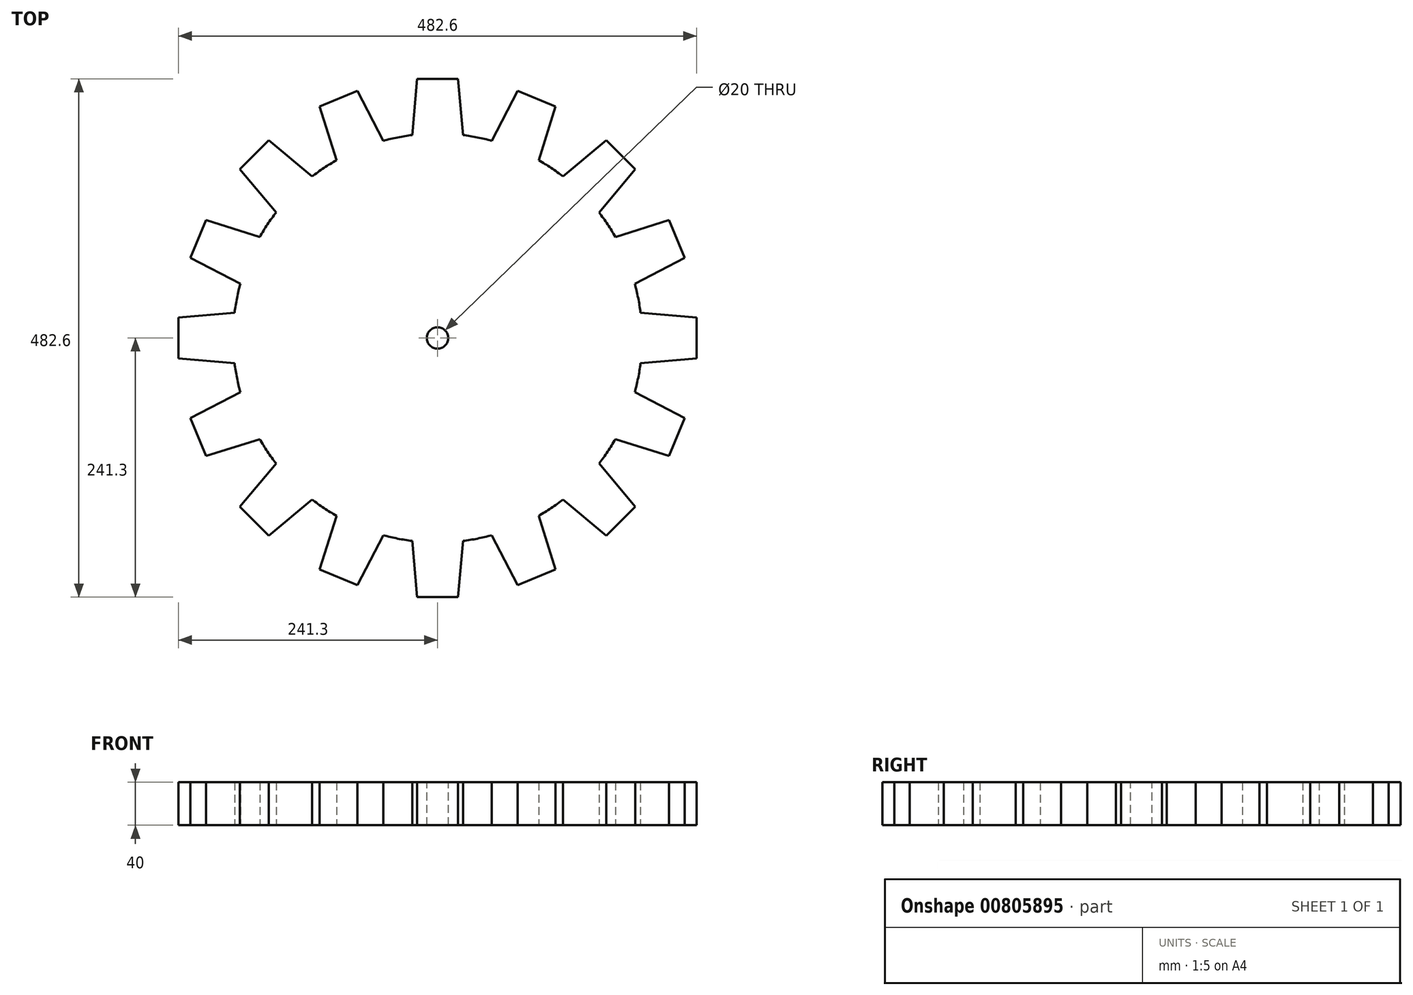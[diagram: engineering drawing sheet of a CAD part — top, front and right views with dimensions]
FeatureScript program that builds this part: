
annotation { "Feature Type Name" : "Feature", "Feature Type Description" : "" }
export const myFeature = defineFeature(function(context is Context, id is Id, definition is map)
    precondition{}
    {
        {
            var Q0;
            Q0=qCreatedBy(makeId("Top.planeOp"),FACE);
            var sketch = newSketch(context, id + "F0", { "sketchPlane" : qUnion([Q0])});
            skCircle(sketch, "E0", {"center": v(0, 0) * mm, "radius": 190.5 * mm});
            skLineSegment(sketch, "E1", {"start": v(0, 0) * mm, "end": v(0, 190.5) * mm, "construction": true});
            skLineSegment(sketch, "E2", {"start": v(-23.62, 189.03) * mm, "end": v(-19.05, 241.3) * mm});
            skLineSegment(sketch, "E3", {"start": v(-19.05, 241.3) * mm, "end": v(0, 241.3) * mm});
            skLineSegment(sketch, "E4.MirrorCS", {"start": v(23.62, 189.03) * mm, "end": v(19.05, 241.3) * mm});
            skLineSegment(sketch, "E5.MirrorCS", {"start": v(19.05, 241.3) * mm, "end": v(0, 241.3) * mm});
            skLineSegment(sketch, "E6.1.0", {"start": v(-94.16, 165.6) * mm, "end": v(-109.94, 215.64) * mm});
            skLineSegment(sketch, "E6.1.1", {"start": v(-109.94, 215.64) * mm, "end": v(-92.34, 222.93) * mm});
            skLineSegment(sketch, "E6.1.2", {"start": v(-74.74, 230.22) * mm, "end": v(-92.34, 222.93) * mm});
            skLineSegment(sketch, "E6.1.3", {"start": v(-50.51, 183.68) * mm, "end": v(-74.74, 230.22) * mm});
            skLineSegment(sketch, "E6.2.0", {"start": v(-150.37, 116.96) * mm, "end": v(-184.1, 157.15) * mm});
            skLineSegment(sketch, "E6.2.1", {"start": v(-184.1, 157.15) * mm, "end": v(-170.62, 170.62) * mm});
            skLineSegment(sketch, "E6.2.2", {"start": v(-157.15, 184.1) * mm, "end": v(-170.62, 170.62) * mm});
            skLineSegment(sketch, "E6.2.3", {"start": v(-116.96, 150.37) * mm, "end": v(-157.15, 184.1) * mm});
            skLineSegment(sketch, "E6.3.0", {"start": v(-183.68, 50.51) * mm, "end": v(-230.22, 74.74) * mm});
            skLineSegment(sketch, "E6.3.1", {"start": v(-230.22, 74.74) * mm, "end": v(-222.93, 92.34) * mm});
            skLineSegment(sketch, "E6.3.2", {"start": v(-215.64, 109.94) * mm, "end": v(-222.93, 92.34) * mm});
            skLineSegment(sketch, "E6.3.3", {"start": v(-165.6, 94.16) * mm, "end": v(-215.64, 109.94) * mm});
            skLineSegment(sketch, "E6.4.0", {"start": v(-189.03, -23.62) * mm, "end": v(-241.3, -19.05) * mm});
            skLineSegment(sketch, "E6.4.1", {"start": v(-241.3, -19.05) * mm, "end": v(-241.3, 0) * mm});
            skLineSegment(sketch, "E6.4.2", {"start": v(-241.3, 19.05) * mm, "end": v(-241.3, 0) * mm});
            skLineSegment(sketch, "E6.4.3", {"start": v(-189.03, 23.62) * mm, "end": v(-241.3, 19.05) * mm});
            skLineSegment(sketch, "E6.5.0", {"start": v(-165.6, -94.16) * mm, "end": v(-215.64, -109.94) * mm});
            skLineSegment(sketch, "E6.5.1", {"start": v(-215.64, -109.94) * mm, "end": v(-222.93, -92.34) * mm});
            skLineSegment(sketch, "E6.5.2", {"start": v(-230.22, -74.74) * mm, "end": v(-222.93, -92.34) * mm});
            skLineSegment(sketch, "E6.5.3", {"start": v(-183.68, -50.51) * mm, "end": v(-230.22, -74.74) * mm});
            skLineSegment(sketch, "E6.6.0", {"start": v(-116.96, -150.37) * mm, "end": v(-157.15, -184.1) * mm});
            skLineSegment(sketch, "E6.6.1", {"start": v(-157.15, -184.1) * mm, "end": v(-170.62, -170.62) * mm});
            skLineSegment(sketch, "E6.6.2", {"start": v(-184.1, -157.15) * mm, "end": v(-170.62, -170.62) * mm});
            skLineSegment(sketch, "E6.6.3", {"start": v(-150.37, -116.96) * mm, "end": v(-184.1, -157.15) * mm});
            skLineSegment(sketch, "E6.7.0", {"start": v(-50.51, -183.68) * mm, "end": v(-74.74, -230.22) * mm});
            skLineSegment(sketch, "E6.7.1", {"start": v(-74.74, -230.22) * mm, "end": v(-92.34, -222.93) * mm});
            skLineSegment(sketch, "E6.7.2", {"start": v(-109.94, -215.64) * mm, "end": v(-92.34, -222.93) * mm});
            skLineSegment(sketch, "E6.7.3", {"start": v(-94.16, -165.6) * mm, "end": v(-109.94, -215.64) * mm});
            skLineSegment(sketch, "E6.8.0", {"start": v(23.62, -189.03) * mm, "end": v(19.05, -241.3) * mm});
            skLineSegment(sketch, "E6.8.1", {"start": v(19.05, -241.3) * mm, "end": v(0, -241.3) * mm});
            skLineSegment(sketch, "E6.8.2", {"start": v(-19.05, -241.3) * mm, "end": v(0, -241.3) * mm});
            skLineSegment(sketch, "E6.8.3", {"start": v(-23.62, -189.03) * mm, "end": v(-19.05, -241.3) * mm});
            skLineSegment(sketch, "E6.9.0", {"start": v(94.16, -165.6) * mm, "end": v(109.94, -215.64) * mm});
            skLineSegment(sketch, "E6.9.1", {"start": v(109.94, -215.64) * mm, "end": v(92.34, -222.93) * mm});
            skLineSegment(sketch, "E6.9.2", {"start": v(74.74, -230.22) * mm, "end": v(92.34, -222.93) * mm});
            skLineSegment(sketch, "E6.9.3", {"start": v(50.51, -183.68) * mm, "end": v(74.74, -230.22) * mm});
            skLineSegment(sketch, "E6.10.0", {"start": v(150.37, -116.96) * mm, "end": v(184.1, -157.15) * mm});
            skLineSegment(sketch, "E6.10.1", {"start": v(184.1, -157.15) * mm, "end": v(170.62, -170.62) * mm});
            skLineSegment(sketch, "E6.10.2", {"start": v(157.15, -184.1) * mm, "end": v(170.62, -170.62) * mm});
            skLineSegment(sketch, "E6.10.3", {"start": v(116.96, -150.37) * mm, "end": v(157.15, -184.1) * mm});
            skLineSegment(sketch, "E6.11.0", {"start": v(183.68, -50.51) * mm, "end": v(230.22, -74.74) * mm});
            skLineSegment(sketch, "E6.11.1", {"start": v(230.22, -74.74) * mm, "end": v(222.93, -92.34) * mm});
            skLineSegment(sketch, "E6.11.2", {"start": v(215.64, -109.94) * mm, "end": v(222.93, -92.34) * mm});
            skLineSegment(sketch, "E6.11.3", {"start": v(165.6, -94.16) * mm, "end": v(215.64, -109.94) * mm});
            skLineSegment(sketch, "E6.12.0", {"start": v(189.03, 23.62) * mm, "end": v(241.3, 19.05) * mm});
            skLineSegment(sketch, "E6.12.1", {"start": v(241.3, 19.05) * mm, "end": v(241.3, 0) * mm});
            skLineSegment(sketch, "E6.12.2", {"start": v(241.3, -19.05) * mm, "end": v(241.3, 0) * mm});
            skLineSegment(sketch, "E6.12.3", {"start": v(189.03, -23.62) * mm, "end": v(241.3, -19.05) * mm});
            skLineSegment(sketch, "E6.13.0", {"start": v(165.6, 94.16) * mm, "end": v(215.64, 109.94) * mm});
            skLineSegment(sketch, "E6.13.1", {"start": v(215.64, 109.94) * mm, "end": v(222.93, 92.34) * mm});
            skLineSegment(sketch, "E6.13.2", {"start": v(230.22, 74.74) * mm, "end": v(222.93, 92.34) * mm});
            skLineSegment(sketch, "E6.13.3", {"start": v(183.68, 50.51) * mm, "end": v(230.22, 74.74) * mm});
            skLineSegment(sketch, "E6.14.0", {"start": v(116.96, 150.37) * mm, "end": v(157.15, 184.1) * mm});
            skLineSegment(sketch, "E6.14.1", {"start": v(157.15, 184.1) * mm, "end": v(170.62, 170.62) * mm});
            skLineSegment(sketch, "E6.14.2", {"start": v(184.1, 157.15) * mm, "end": v(170.62, 170.62) * mm});
            skLineSegment(sketch, "E6.14.3", {"start": v(150.37, 116.96) * mm, "end": v(184.1, 157.15) * mm});
            skLineSegment(sketch, "E6.15.0", {"start": v(50.51, 183.68) * mm, "end": v(74.74, 230.22) * mm});
            skLineSegment(sketch, "E6.15.1", {"start": v(74.74, 230.22) * mm, "end": v(92.34, 222.93) * mm});
            skLineSegment(sketch, "E6.15.2", {"start": v(109.94, 215.64) * mm, "end": v(92.34, 222.93) * mm});
            skLineSegment(sketch, "E6.15.3", {"start": v(94.16, 165.6) * mm, "end": v(109.94, 215.64) * mm});
            skSolve(sketch);
        }
        {
            var Q0;
            {var subQ0=sQuery(id+"F0.wireOp",EDGE,"E0");var subQ18=makeQuery(id+"F0.imprint","INTERSECT",VERTEX,{"derivedFrom":[subQ0,sQuery(id+"F0.wireOp",EDGE,"E6.12.0")]});Q0=makeQuery(id+"F0.imprint","IMPRINT",FACE,{"disambiguationData":[TD([[makeQuery(id+"F0.imprint","IMPRINT",EDGE,{"disambiguationData":[TD([[subQ18,-1.0]])],"derivedFrom":subQ0}),1.0]])]});}
            var Q1;
            Q1 = qSketchRegion(id + "F0", true);
            extrude(context, id + "F1", {"entities" : qUnion([Q0, Q1]), "depth" : 20 * mm, "offsetDistance" : 25.4 * mm});
        }
        {
            var Q0;
            Q0=makeQuery(id+"F1.opExtrude","CAP_FACE",FACE,{"disambiguationData":[OSD([sQuery(id+"F0.wireOp",EDGE,"E0"),sQuery(id+"F0.wireOp",EDGE,"E2"),sQuery(id+"F0.wireOp",EDGE,"E3"),sQuery(id+"F0.wireOp",EDGE,"E4.MirrorCS"),sQuery(id+"F0.wireOp",EDGE,"E5.MirrorCS"),sQuery(id+"F0.wireOp",EDGE,"E6.1.0"),sQuery(id+"F0.wireOp",EDGE,"E6.1.1"),sQuery(id+"F0.wireOp",EDGE,"E6.1.2"),sQuery(id+"F0.wireOp",EDGE,"E6.1.3"),sQuery(id+"F0.wireOp",EDGE,"E6.2.0"),sQuery(id+"F0.wireOp",EDGE,"E6.2.1"),sQuery(id+"F0.wireOp",EDGE,"E6.2.2"),sQuery(id+"F0.wireOp",EDGE,"E6.2.3"),sQuery(id+"F0.wireOp",EDGE,"E6.3.0"),sQuery(id+"F0.wireOp",EDGE,"E6.3.1"),sQuery(id+"F0.wireOp",EDGE,"E6.3.2"),sQuery(id+"F0.wireOp",EDGE,"E6.3.3"),sQuery(id+"F0.wireOp",EDGE,"E6.4.0"),sQuery(id+"F0.wireOp",EDGE,"E6.4.1"),sQuery(id+"F0.wireOp",EDGE,"E6.4.2"),sQuery(id+"F0.wireOp",EDGE,"E6.4.3"),sQuery(id+"F0.wireOp",EDGE,"E6.5.0"),sQuery(id+"F0.wireOp",EDGE,"E6.5.1"),sQuery(id+"F0.wireOp",EDGE,"E6.5.2"),sQuery(id+"F0.wireOp",EDGE,"E6.5.3"),sQuery(id+"F0.wireOp",EDGE,"E6.6.0"),sQuery(id+"F0.wireOp",EDGE,"E6.6.1"),sQuery(id+"F0.wireOp",EDGE,"E6.6.2"),sQuery(id+"F0.wireOp",EDGE,"E6.6.3"),sQuery(id+"F0.wireOp",EDGE,"E6.7.0"),sQuery(id+"F0.wireOp",EDGE,"E6.7.1"),sQuery(id+"F0.wireOp",EDGE,"E6.7.2"),sQuery(id+"F0.wireOp",EDGE,"E6.7.3"),sQuery(id+"F0.wireOp",EDGE,"E6.8.0"),sQuery(id+"F0.wireOp",EDGE,"E6.8.1"),sQuery(id+"F0.wireOp",EDGE,"E6.8.2"),sQuery(id+"F0.wireOp",EDGE,"E6.8.3"),sQuery(id+"F0.wireOp",EDGE,"E6.9.0"),sQuery(id+"F0.wireOp",EDGE,"E6.9.1"),sQuery(id+"F0.wireOp",EDGE,"E6.9.2"),sQuery(id+"F0.wireOp",EDGE,"E6.9.3"),sQuery(id+"F0.wireOp",EDGE,"E6.10.0"),sQuery(id+"F0.wireOp",EDGE,"E6.10.1"),sQuery(id+"F0.wireOp",EDGE,"E6.10.2"),sQuery(id+"F0.wireOp",EDGE,"E6.10.3"),sQuery(id+"F0.wireOp",EDGE,"E6.11.0"),sQuery(id+"F0.wireOp",EDGE,"E6.11.1"),sQuery(id+"F0.wireOp",EDGE,"E6.11.2"),sQuery(id+"F0.wireOp",EDGE,"E6.11.3"),sQuery(id+"F0.wireOp",EDGE,"E6.12.0"),sQuery(id+"F0.wireOp",EDGE,"E6.12.1"),sQuery(id+"F0.wireOp",EDGE,"E6.12.2"),sQuery(id+"F0.wireOp",EDGE,"E6.12.3"),sQuery(id+"F0.wireOp",EDGE,"E6.13.0"),sQuery(id+"F0.wireOp",EDGE,"E6.13.1"),sQuery(id+"F0.wireOp",EDGE,"E6.13.2"),sQuery(id+"F0.wireOp",EDGE,"E6.13.3"),sQuery(id+"F0.wireOp",EDGE,"E6.14.0"),sQuery(id+"F0.wireOp",EDGE,"E6.14.1"),sQuery(id+"F0.wireOp",EDGE,"E6.14.2"),sQuery(id+"F0.wireOp",EDGE,"E6.14.3"),sQuery(id+"F0.wireOp",EDGE,"E6.15.0"),sQuery(id+"F0.wireOp",EDGE,"E6.15.1"),sQuery(id+"F0.wireOp",EDGE,"E6.15.2"),sQuery(id+"F0.wireOp",EDGE,"E6.15.3")])],"isStart":false});
            var sketch = newSketch(context, id + "F2", { "sketchPlane" : qUnion([Q0])});
            skCircle(sketch, "E7", {"center": v(0, 0) * mm, "radius": 10 * mm});
            skSolve(sketch);
        }
        {
            var Q0;
            Q0 = qSketchRegion(id + "F2", true);
            extrude(context, id + "F3", {"entities" : qUnion([Q0]), "operationType" : NewBodyOperationType.REMOVE, "endBound" : BoundingType.THROUGH_ALL, "oppositeDirection" : true, "depth" : 25 * mm, "offsetDistance" : 25 * mm});
        }
        {
            var Q0;
            Q0=makeQuery(id+"F1.opExtrude","CAP_FACE",FACE,{"disambiguationData":[OSD([sQuery(id+"F0.wireOp",EDGE,"E0"),sQuery(id+"F0.wireOp",EDGE,"E2"),sQuery(id+"F0.wireOp",EDGE,"E3"),sQuery(id+"F0.wireOp",EDGE,"E4.MirrorCS"),sQuery(id+"F0.wireOp",EDGE,"E5.MirrorCS"),sQuery(id+"F0.wireOp",EDGE,"E6.1.0"),sQuery(id+"F0.wireOp",EDGE,"E6.1.1"),sQuery(id+"F0.wireOp",EDGE,"E6.1.2"),sQuery(id+"F0.wireOp",EDGE,"E6.1.3"),sQuery(id+"F0.wireOp",EDGE,"E6.2.0"),sQuery(id+"F0.wireOp",EDGE,"E6.2.1"),sQuery(id+"F0.wireOp",EDGE,"E6.2.2"),sQuery(id+"F0.wireOp",EDGE,"E6.2.3"),sQuery(id+"F0.wireOp",EDGE,"E6.3.0"),sQuery(id+"F0.wireOp",EDGE,"E6.3.1"),sQuery(id+"F0.wireOp",EDGE,"E6.3.2"),sQuery(id+"F0.wireOp",EDGE,"E6.3.3"),sQuery(id+"F0.wireOp",EDGE,"E6.4.0"),sQuery(id+"F0.wireOp",EDGE,"E6.4.1"),sQuery(id+"F0.wireOp",EDGE,"E6.4.2"),sQuery(id+"F0.wireOp",EDGE,"E6.4.3"),sQuery(id+"F0.wireOp",EDGE,"E6.5.0"),sQuery(id+"F0.wireOp",EDGE,"E6.5.1"),sQuery(id+"F0.wireOp",EDGE,"E6.5.2"),sQuery(id+"F0.wireOp",EDGE,"E6.5.3"),sQuery(id+"F0.wireOp",EDGE,"E6.6.0"),sQuery(id+"F0.wireOp",EDGE,"E6.6.1"),sQuery(id+"F0.wireOp",EDGE,"E6.6.2"),sQuery(id+"F0.wireOp",EDGE,"E6.6.3"),sQuery(id+"F0.wireOp",EDGE,"E6.7.0"),sQuery(id+"F0.wireOp",EDGE,"E6.7.1"),sQuery(id+"F0.wireOp",EDGE,"E6.7.2"),sQuery(id+"F0.wireOp",EDGE,"E6.7.3"),sQuery(id+"F0.wireOp",EDGE,"E6.8.0"),sQuery(id+"F0.wireOp",EDGE,"E6.8.1"),sQuery(id+"F0.wireOp",EDGE,"E6.8.2"),sQuery(id+"F0.wireOp",EDGE,"E6.8.3"),sQuery(id+"F0.wireOp",EDGE,"E6.9.0"),sQuery(id+"F0.wireOp",EDGE,"E6.9.1"),sQuery(id+"F0.wireOp",EDGE,"E6.9.2"),sQuery(id+"F0.wireOp",EDGE,"E6.9.3"),sQuery(id+"F0.wireOp",EDGE,"E6.10.0"),sQuery(id+"F0.wireOp",EDGE,"E6.10.1"),sQuery(id+"F0.wireOp",EDGE,"E6.10.2"),sQuery(id+"F0.wireOp",EDGE,"E6.10.3"),sQuery(id+"F0.wireOp",EDGE,"E6.11.0"),sQuery(id+"F0.wireOp",EDGE,"E6.11.1"),sQuery(id+"F0.wireOp",EDGE,"E6.11.2"),sQuery(id+"F0.wireOp",EDGE,"E6.11.3"),sQuery(id+"F0.wireOp",EDGE,"E6.12.0"),sQuery(id+"F0.wireOp",EDGE,"E6.12.1"),sQuery(id+"F0.wireOp",EDGE,"E6.12.2"),sQuery(id+"F0.wireOp",EDGE,"E6.12.3"),sQuery(id+"F0.wireOp",EDGE,"E6.13.0"),sQuery(id+"F0.wireOp",EDGE,"E6.13.1"),sQuery(id+"F0.wireOp",EDGE,"E6.13.2"),sQuery(id+"F0.wireOp",EDGE,"E6.13.3"),sQuery(id+"F0.wireOp",EDGE,"E6.14.0"),sQuery(id+"F0.wireOp",EDGE,"E6.14.1"),sQuery(id+"F0.wireOp",EDGE,"E6.14.2"),sQuery(id+"F0.wireOp",EDGE,"E6.14.3"),sQuery(id+"F0.wireOp",EDGE,"E6.15.0"),sQuery(id+"F0.wireOp",EDGE,"E6.15.1"),sQuery(id+"F0.wireOp",EDGE,"E6.15.2"),sQuery(id+"F0.wireOp",EDGE,"E6.15.3")])],"isStart":false});
            extrude(context, id + "F4", {"entities" : qUnion([Q0]), "operationType" : NewBodyOperationType.ADD, "depth" : 20 * mm, "offsetDistance" : 25 * mm});
        }
    });
